# Revit family: Mirror-LED_Sidelit-Bobrick-B-164_Series
name_source: partatom
category: Furniture
units: mm (PartAtom-declared; Revit-internal decimal feet)

## family parameters
Cut with Voids When Loaded = No
Host = Face
OmniClass Number = 23.40.95.17.17
OmniClass Title = Mirrors
Room Calculation Point = No
Shared = Yes

## types (2) — shared parameters
ADA Compliant = Yes
Apparent Load = 0 VA
Assembly Code = E2010
Default Elevation = 40"
Description = B-164 Series 
LED Backlit Mirror
Commercial grade mirror construction combined with LED-lights reflecting quality, value and style. Mirror and mounting panel is IP44 rated, lead free silver backing exceeds ISO 9227:201, 120 hour corrosion testing. Light engine is IP66 rated with 50,000 hours estimated life. Dimming option. 30” cord with three-prong plug 6mm safety film backed glass mirror, with backside aluminum frame with key lock holes, for wall mounted installation.
Frame Material = Metal-Bobrick-Aluminum
Installation Type = Wall Mounted
Lamp = LED
Length = 1 3/4"
Manufacturer = Bobrick
Mirror Material = Mirror-Bobrick
Mounting Panel Material = Metal-Bobrick-Aluminum
Price = Prices may vary. Please consult Manufacturer Representative for most up-to-date price list.
Product Documentation Link = https://www.bobrick.com
Product Page URL = https://www.bobrick.com
URL = http://bobrick.com
Voltage = 24 V
Width = 24"

## per-type parameters (varying)
| type | Height | Lumens | Watts |
| B-164 2436 | 36" | 2,500 | 36 W |
| B-164 2442 | 42" | 2,900 | 40 W |

note: column(s) folded — value = type name in every type: Model

## geometry (parser evidence)
native form markers: Sweep x2
no freeform markers — native parametric forms only
